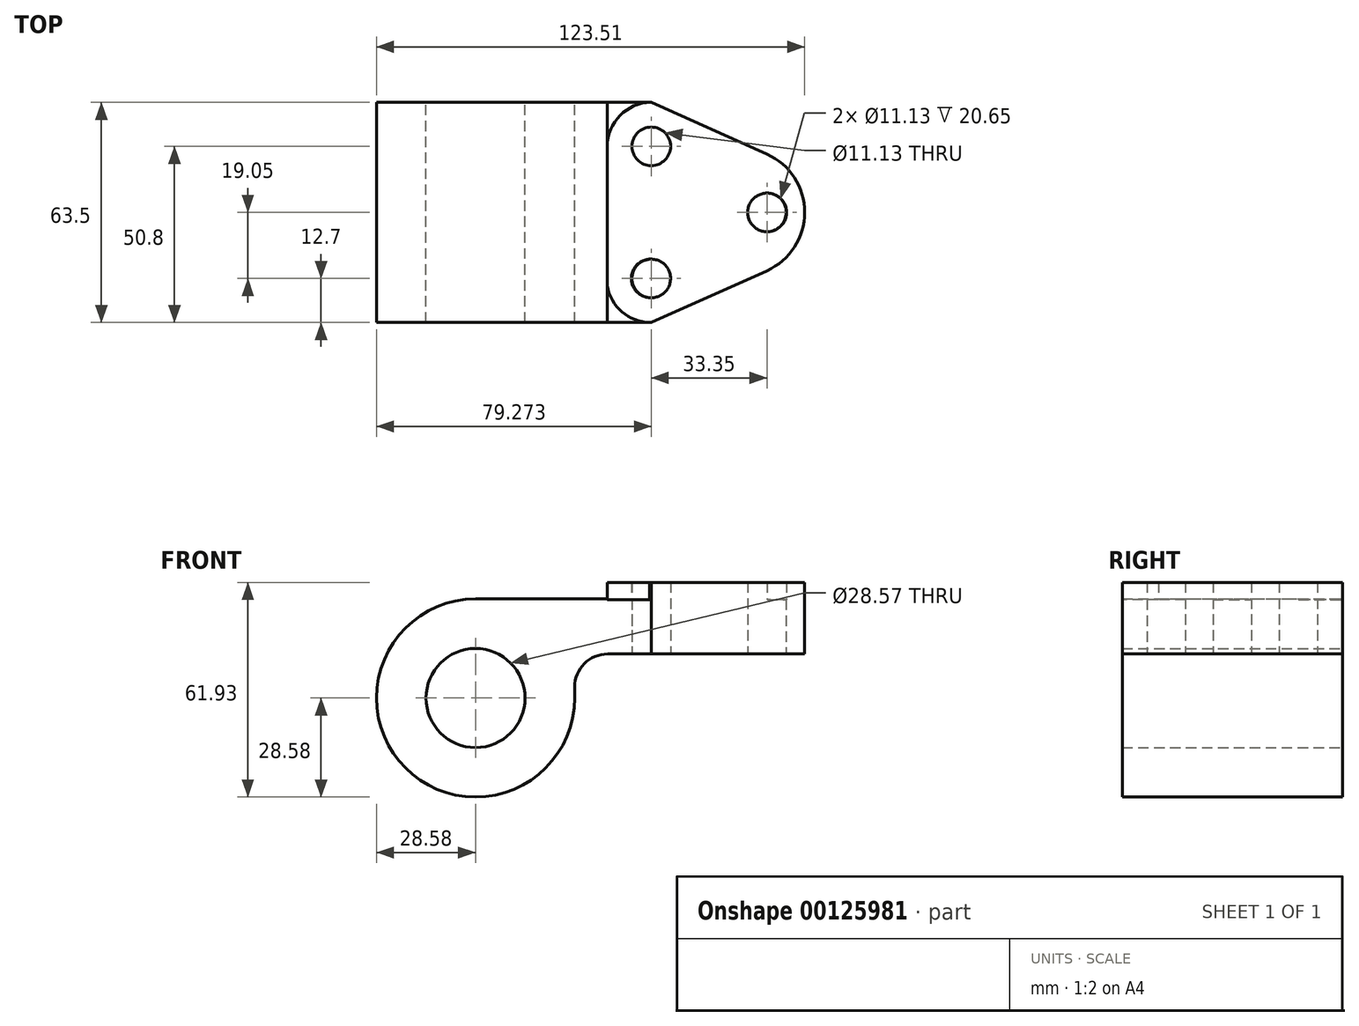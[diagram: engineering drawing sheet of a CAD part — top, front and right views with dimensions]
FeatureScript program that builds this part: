
annotation { "Feature Type Name" : "Feature", "Feature Type Description" : "" }
export const myFeature = defineFeature(function(context is Context, id is Id, definition is map)
    precondition{}
    {
        {
            var Q0;
            Q0=qCreatedBy(makeId("Front.planeOp"),FACE);
            var sketch = newSketch(context, id + "F0", { "sketchPlane" : qUnion([Q0])});
            skCircle(sketch, "E0", {"center": v(0, 0) * mm, "radius": 14.29 * mm});
            skLineSegment(sketch, "E1", {"start": v(0, 28.58) * mm, "end": v(38, 28.58) * mm});
            skLineSegment(sketch, "E2", {"start": v(38, 28.58) * mm, "end": v(38, 33.35) * mm});
            skLineSegment(sketch, "E3", {"start": v(38, 33.35) * mm, "end": v(95.03, 33.35) * mm});
            skLineSegment(sketch, "E4", {"start": v(95.03, 33.35) * mm, "end": v(95.03, 12.7) * mm});
            skLineSegment(sketch, "E5", {"start": v(95.03, 12.7) * mm, "end": v(69.85, 12.7) * mm});
            skArc(sketch, "E6", {"start": v(0, 28.58) * mm, "mid": v(-20.2, -20.2) * mm, "end": v(28.58, 0) * mm});
            skLineSegment(sketch, "E7", {"start": v(28.58, 0) * mm, "end": v(28.58, 3.17) * mm});
            skLineSegment(sketch, "E8", {"start": v(38.1, 12.7) * mm, "end": v(69.85, 12.7) * mm});
            skPoint(sketch, "E9.visualSharp", {"position": v(28.58, 12.7) * mm});
            skArc(sketch, "E9.filletArc", {"start": v(38.1, 12.7) * mm, "mid": v(31.36, 9.91) * mm, "end": v(28.58, 3.17) * mm});
            skSolve(sketch);
        }
        {
            var Q0;
            Q0 = qSketchRegion(id + "F0", true);
            extrude(context, id + "F1", {"entities" : qUnion([Q0]), "depth" : 63.5 * mm});
        }
        {
            var Q0;
            Q0=qCreatedBy(makeId("Top.planeOp"),FACE);
            var sketch = newSketch(context, id + "F2", { "sketchPlane" : qUnion([Q0])});
            skLineSegment(sketch, "E10", {"start": v(50.8, -63.5) * mm, "end": v(84.15, -48.56) * mm});
            skCircle(sketch, "E11", {"center": v(84.15, -31.75) * mm, "radius": 5.56 * mm});
            skCircle(sketch, "E12", {"center": v(50.7, -12.7) * mm, "radius": 5.56 * mm});
            skCircle(sketch, "E13", {"center": v(50.5, -50.8) * mm, "radius": 5.56 * mm});
            skPoint(sketch, "E14.visualSharp", {"position": v(38, 0) * mm});
            skArc(sketch, "E14.filletArc", {"start": v(50.8, 0) * mm, "mid": v(41.75, -3.68) * mm, "end": v(38, -12.7) * mm});
            skArc(sketch, "E15", {"start": v(38, -52.98) * mm, "mid": v(42.44, -60.62) * mm, "end": v(50.8, -63.5) * mm});
            skLineSegment(sketch, "E16", {"start": v(50.8, 0) * mm, "end": v(84.15, -14.94) * mm});
            skArc(sketch, "E17", {"start": v(84.15, -48.56) * mm, "mid": v(95.03, -31.75) * mm, "end": v(84.15, -14.94) * mm});
            skLineSegment(sketch, "E18", {"start": v(50.8, 0) * mm, "end": v(38, 0) * mm});
            skLineSegment(sketch, "E19", {"start": v(38, -12.7) * mm, "end": v(38, 0) * mm});
            skLineSegment(sketch, "E20", {"start": v(38, -52.98) * mm, "end": v(38, -63.5) * mm});
            skLineSegment(sketch, "E21", {"start": v(38, -63.5) * mm, "end": v(50.8, -63.5) * mm});
            skSolve(sketch);
        }
        {
            var Q0;
            Q0 = qSketchRegion(id + "F2", true);
            var Q1;
            Q1=makeQuery(id+"F1.opExtrude","SWEPT_FACE",FACE,{"disambiguationData":[OSD([sQuery(id+"F0.wireOp",EDGE,"E3")])]});
            extrude(context, id + "F3", {"entities" : qUnion([Q0]), "operationType" : NewBodyOperationType.REMOVE, "endBound" : BoundingType.UP_TO_SURFACE, "endBoundEntityFace" : qUnion([Q1]), "depth" : 25.4 * mm, "hasSecondDirection" : true, "secondDirectionOppositeDirection" : false, "secondDirectionDepth" : 28.4 * mm});
        }
        {
            var Q0;
            Q0=qCreatedBy(makeId("Top.planeOp"),FACE);
            var sketch = newSketch(context, id + "F4", { "sketchPlane" : qUnion([Q0])});
            skLineSegment(sketch, "E22", {"start": v(50.7, -63.5) * mm, "end": v(84.04, -48.56) * mm});
            skCircle(sketch, "E23", {"center": v(84.04, -31.75) * mm, "radius": 5.56 * mm});
            skCircle(sketch, "E24", {"center": v(50.7, -12.7) * mm, "radius": 5.56 * mm});
            skCircle(sketch, "E25", {"center": v(50.7, -50.8) * mm, "radius": 5.56 * mm});
            skPoint(sketch, "E26.visualSharp", {"position": v(38, 0) * mm});
            skArc(sketch, "E26.filletArc", {"start": v(50.7, 0) * mm, "mid": v(41.71, -3.72) * mm, "end": v(38, -12.7) * mm});
            skArc(sketch, "E27", {"start": v(38.18, -52.97) * mm, "mid": v(42.52, -60.52) * mm, "end": v(50.7, -63.5) * mm});
            skLineSegment(sketch, "E28", {"start": v(50.7, 0) * mm, "end": v(84.04, -14.94) * mm});
            skArc(sketch, "E29", {"start": v(84.04, -48.56) * mm, "mid": v(94.93, -31.75) * mm, "end": v(84.04, -14.94) * mm});
            skLineSegment(sketch, "E30", {"start": v(50.7, 0) * mm, "end": v(95.03, 0) * mm});
            skLineSegment(sketch, "E31", {"start": v(50.7, -63.5) * mm, "end": v(95.03, -63.5) * mm});
            skLineSegment(sketch, "E32", {"start": v(95.03, 0) * mm, "end": v(95.03, -63.5) * mm});
            skSolve(sketch);
        }
        {
            var Q0;
            Q0 = qSketchRegion(id + "F4", true);
            extrude(context, id + "F5", {"entities" : qUnion([Q0]), "operationType" : NewBodyOperationType.REMOVE, "endBound" : BoundingType.THROUGH_ALL, "depth" : 25.4 * mm});
        }
    });
